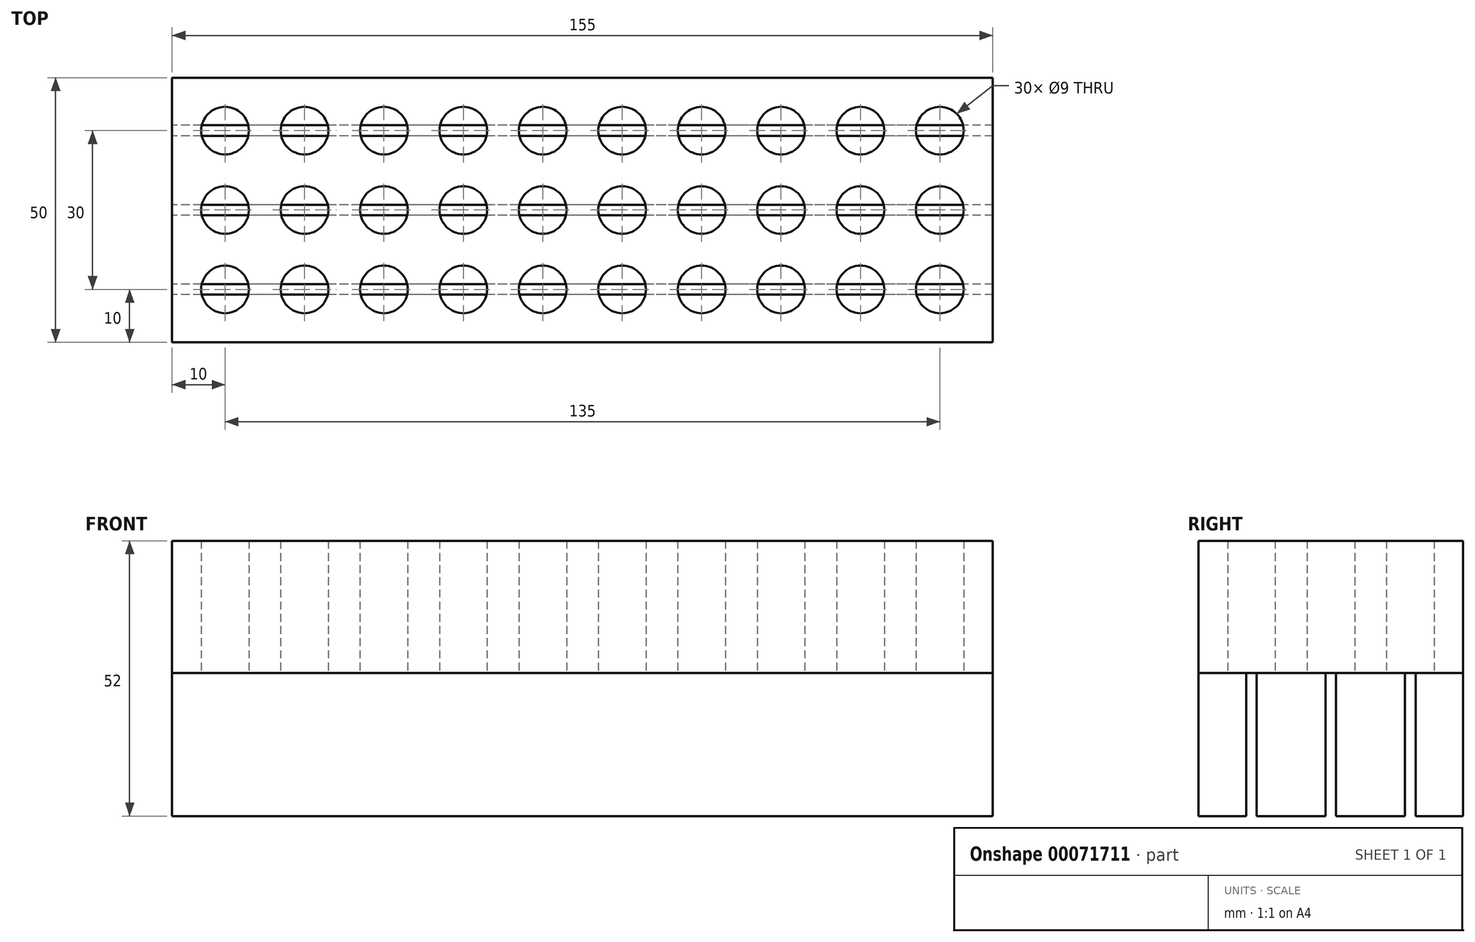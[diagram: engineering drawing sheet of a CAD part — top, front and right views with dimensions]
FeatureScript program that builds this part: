
annotation { "Feature Type Name" : "Feature", "Feature Type Description" : "" }
export const myFeature = defineFeature(function(context is Context, id is Id, definition is map)
    precondition{}
    {
        {
            var Q0;
            Q0=qCreatedBy(makeId("Top.planeOp"),FACE);
            var sketch = newSketch(context, id + "F0", { "sketchPlane" : qUnion([Q0])});
            skLineSegment(sketch, "E0.rect.bottom", {"start": v(77.5, 25) * mm, "end": v(-77.5, 25) * mm});
            skLineSegment(sketch, "E0.rect.top", {"start": v(77.5, -25) * mm, "end": v(-77.5, -25) * mm});
            skLineSegment(sketch, "E0.rect.left", {"start": v(77.5, 25) * mm, "end": v(77.5, -25) * mm});
            skLineSegment(sketch, "E0.rect.right", {"start": v(-77.5, 25) * mm, "end": v(-77.5, -25) * mm});
            skPoint(sketch, "E0.rect.middle", {"position": v(0, 0) * mm});
            skCircle(sketch, "E1", {"center": v(-67.5, 15) * mm, "radius": 4.5 * mm, "construction": true});
            skLineSegment(sketch, "E2.rect.bottom", {"start": v(77.5, 1) * mm, "end": v(-77.5, 1) * mm});
            skLineSegment(sketch, "E2.rect.top", {"start": v(77.5, -1) * mm, "end": v(-77.5, -1) * mm});
            skLineSegment(sketch, "E2.rect.left", {"start": v(77.5, 1) * mm, "end": v(77.5, -1) * mm});
            skLineSegment(sketch, "E2.rect.right", {"start": v(-77.5, 1) * mm, "end": v(-77.5, -1) * mm});
            skCircle(sketch, "E3.0.1.0", {"center": v(-67.5, 0) * mm, "radius": 4.5 * mm, "construction": true});
            skCircle(sketch, "E3.0.2.0", {"center": v(-67.5, -15) * mm, "radius": 4.5 * mm, "construction": true});
            skCircle(sketch, "E3.1.0.0", {"center": v(-52.5, 15) * mm, "radius": 4.5 * mm, "construction": true});
            skCircle(sketch, "E3.1.1.0", {"center": v(-52.5, 0) * mm, "radius": 4.5 * mm, "construction": true});
            skCircle(sketch, "E3.1.2.0", {"center": v(-52.5, -15) * mm, "radius": 4.5 * mm, "construction": true});
            skCircle(sketch, "E3.2.0.0", {"center": v(-37.5, 15) * mm, "radius": 4.5 * mm, "construction": true});
            skCircle(sketch, "E3.2.1.0", {"center": v(-37.5, 0) * mm, "radius": 4.5 * mm, "construction": true});
            skCircle(sketch, "E3.2.2.0", {"center": v(-37.5, -15) * mm, "radius": 4.5 * mm, "construction": true});
            skCircle(sketch, "E3.3.0.0", {"center": v(-22.5, 15) * mm, "radius": 4.5 * mm, "construction": true});
            skCircle(sketch, "E3.3.1.0", {"center": v(-22.5, 0) * mm, "radius": 4.5 * mm, "construction": true});
            skCircle(sketch, "E3.3.2.0", {"center": v(-22.5, -15) * mm, "radius": 4.5 * mm, "construction": true});
            skCircle(sketch, "E3.4.0.0", {"center": v(-7.5, 15) * mm, "radius": 4.5 * mm, "construction": true});
            skCircle(sketch, "E3.4.1.0", {"center": v(-7.5, 0) * mm, "radius": 4.5 * mm, "construction": true});
            skCircle(sketch, "E3.4.2.0", {"center": v(-7.5, -15) * mm, "radius": 4.5 * mm, "construction": true});
            skCircle(sketch, "E3.5.0.0", {"center": v(7.5, 15) * mm, "radius": 4.5 * mm, "construction": true});
            skCircle(sketch, "E3.5.1.0", {"center": v(7.5, 0) * mm, "radius": 4.5 * mm, "construction": true});
            skCircle(sketch, "E3.5.2.0", {"center": v(7.5, -15) * mm, "radius": 4.5 * mm, "construction": true});
            skCircle(sketch, "E3.6.0.0", {"center": v(22.5, 15) * mm, "radius": 4.5 * mm, "construction": true});
            skCircle(sketch, "E3.6.1.0", {"center": v(22.5, 0) * mm, "radius": 4.5 * mm, "construction": true});
            skCircle(sketch, "E3.6.2.0", {"center": v(22.5, -15) * mm, "radius": 4.5 * mm, "construction": true});
            skCircle(sketch, "E3.7.0.0", {"center": v(37.5, 15) * mm, "radius": 4.5 * mm, "construction": true});
            skCircle(sketch, "E3.7.1.0", {"center": v(37.5, 0) * mm, "radius": 4.5 * mm, "construction": true});
            skCircle(sketch, "E3.7.2.0", {"center": v(37.5, -15) * mm, "radius": 4.5 * mm, "construction": true});
            skCircle(sketch, "E3.8.0.0", {"center": v(52.5, 15) * mm, "radius": 4.5 * mm, "construction": true});
            skCircle(sketch, "E3.8.1.0", {"center": v(52.5, 0) * mm, "radius": 4.5 * mm, "construction": true});
            skCircle(sketch, "E3.8.2.0", {"center": v(52.5, -15) * mm, "radius": 4.5 * mm, "construction": true});
            skCircle(sketch, "E3.9.0.0", {"center": v(67.5, 15) * mm, "radius": 4.5 * mm, "construction": true});
            skCircle(sketch, "E3.9.1.0", {"center": v(67.5, 0) * mm, "radius": 4.5 * mm, "construction": true});
            skCircle(sketch, "E3.9.2.0", {"center": v(67.5, -15) * mm, "radius": 4.5 * mm, "construction": true});
            skLineSegment(sketch, "E3.direction1", {"start": v(-67.5, 15) * mm, "end": v(-52.5, 15) * mm, "construction": true});
            skLineSegment(sketch, "E3.direction2", {"start": v(-67.5, 15) * mm, "end": v(-67.5, 0) * mm, "construction": true});
            skLineSegment(sketch, "E4.rect.bottom", {"start": v(77.5, 14) * mm, "end": v(-77.5, 14) * mm});
            skLineSegment(sketch, "E4.rect.top", {"start": v(77.5, 16) * mm, "end": v(-77.5, 16) * mm});
            skLineSegment(sketch, "E4.rect.left", {"start": v(77.5, 14) * mm, "end": v(77.5, 16) * mm});
            skLineSegment(sketch, "E4.rect.right", {"start": v(-77.5, 14) * mm, "end": v(-77.5, 16) * mm});
            skPoint(sketch, "E4.rect.middle", {"position": v(0, 15) * mm});
            skPoint(sketch, "E4.rect.middle.positionSnap0", {"position": v(0, 25) * mm});
            skPoint(sketch, "E4.rect.centerSnap0", {"position": v(0, 25) * mm});
            skLineSegment(sketch, "E5.rect.bottom", {"start": v(77.5, -16) * mm, "end": v(-77.5, -16) * mm});
            skLineSegment(sketch, "E5.rect.top", {"start": v(77.5, -14) * mm, "end": v(-77.5, -14) * mm});
            skLineSegment(sketch, "E5.rect.left", {"start": v(77.5, -16) * mm, "end": v(77.5, -14) * mm});
            skLineSegment(sketch, "E5.rect.right", {"start": v(-77.5, -16) * mm, "end": v(-77.5, -14) * mm});
            skPoint(sketch, "E5.rect.middle", {"position": v(0, -15) * mm});
            skPoint(sketch, "E5.rect.middle.positionSnap0", {"position": v(0, -25) * mm});
            skPoint(sketch, "E5.rect.centerSnap0", {"position": v(0, -25) * mm});
            skSolve(sketch);
        }
        {
            var Q0;
            {var subQ0=sQuery(id+"F0.wireOp",EDGE,"E0.rect.bottom");Q0=makeQuery(id+"F0.imprint","IMPRINT",FACE,{"disambiguationData":[TD([[makeQuery(id+"F0.imprint","IMPRINT",EDGE,{"derivedFrom":subQ0}),1.0]])]});}
            var Q1;
            {var subQ0=sQuery(id+"F0.wireOp",EDGE,"E0.rect.top");Q1=makeQuery(id+"F0.imprint","IMPRINT",FACE,{"disambiguationData":[TD([[makeQuery(id+"F0.imprint","IMPRINT",EDGE,{"derivedFrom":subQ0}),-1.0]])]});}
            var Q2;
            {var subQ0=sQuery(id+"F0.wireOp",EDGE,"E2.rect.bottom");Q2=makeQuery(id+"F0.imprint","IMPRINT",FACE,{"disambiguationData":[TD([[makeQuery(id+"F0.imprint","IMPRINT",EDGE,{"derivedFrom":subQ0}),-1.0]])]});}
            var Q3;
            {var subQ0=sQuery(id+"F0.wireOp",EDGE,"E2.rect.top");Q3=makeQuery(id+"F0.imprint","IMPRINT",FACE,{"disambiguationData":[TD([[makeQuery(id+"F0.imprint","IMPRINT",EDGE,{"derivedFrom":subQ0}),1.0]])]});}
            extrude(context, id + "F1", {"entities" : qUnion([Q0, Q1, Q2, Q3]), "depth" : 27 * mm});
        }
        {
            var Q0;
            Q0=makeQuery(id+"F1.opExtrude","CAP_FACE",FACE,{"disambiguationData":[OSD([sQuery(id+"F0.wireOp",EDGE,"E0.rect.left"),sQuery(id+"F0.wireOp",EDGE,"E0.rect.right"),sQuery(id+"F0.wireOp",EDGE,"E2.rect.bottom"),sQuery(id+"F0.wireOp",EDGE,"E4.rect.bottom")])],"isStart":false});
            var sketch = newSketch(context, id + "F2", { "sketchPlane" : qUnion([Q0])});
            skLineSegment(sketch, "E6.0.0", {"start": v(-77.5, -25) * mm, "end": v(77.5, -25) * mm});
            skLineSegment(sketch, "E6.0.1", {"start": v(77.5, -25) * mm, "end": v(77.5, -16) * mm});
            skLineSegment(sketch, "E6.0.3", {"start": v(-77.5, -16) * mm, "end": v(-77.5, -25) * mm});
            skLineSegment(sketch, "E7.0.0", {"start": v(77.5, -14) * mm, "end": v(77.5, -1) * mm});
            skLineSegment(sketch, "E7.0.2", {"start": v(-77.5, -1) * mm, "end": v(-77.5, -14) * mm});
            skLineSegment(sketch, "E8.0.0", {"start": v(77.5, 1) * mm, "end": v(77.5, 14) * mm});
            skLineSegment(sketch, "E8.0.2", {"start": v(-77.5, 14) * mm, "end": v(-77.5, 1) * mm});
            skLineSegment(sketch, "E9.0.0", {"start": v(77.5, 16) * mm, "end": v(77.5, 25) * mm});
            skLineSegment(sketch, "E9.0.1", {"start": v(77.5, 25) * mm, "end": v(-77.5, 25) * mm});
            skLineSegment(sketch, "E9.0.2", {"start": v(-77.5, 25) * mm, "end": v(-77.5, 16) * mm});
            skCircle(sketch, "E10.0", {"center": v(-67.5, 15) * mm, "radius": 4.5 * mm});
            skCircle(sketch, "E11.0", {"center": v(-67.5, 0) * mm, "radius": 4.5 * mm});
            skCircle(sketch, "E12.0", {"center": v(-67.5, -15) * mm, "radius": 4.5 * mm});
            skCircle(sketch, "E13.0", {"center": v(-52.5, -15) * mm, "radius": 4.5 * mm});
            skCircle(sketch, "E14.0", {"center": v(-52.5, 15) * mm, "radius": 4.5 * mm});
            skCircle(sketch, "E15.0", {"center": v(-37.5, -15) * mm, "radius": 4.5 * mm});
            skCircle(sketch, "E16.0", {"center": v(-52.5, 0) * mm, "radius": 4.5 * mm});
            skCircle(sketch, "E17.0", {"center": v(-37.5, 0) * mm, "radius": 4.5 * mm});
            skCircle(sketch, "E18.0", {"center": v(-37.5, 15) * mm, "radius": 4.5 * mm});
            skCircle(sketch, "E19.0", {"center": v(-22.5, 15) * mm, "radius": 4.5 * mm});
            skCircle(sketch, "E20.0", {"center": v(-22.5, 0) * mm, "radius": 4.5 * mm});
            skCircle(sketch, "E21.0", {"center": v(-22.5, -15) * mm, "radius": 4.5 * mm});
            skCircle(sketch, "E22.0", {"center": v(-7.5, -15) * mm, "radius": 4.5 * mm});
            skCircle(sketch, "E23.0", {"center": v(-7.5, 0) * mm, "radius": 4.5 * mm});
            skCircle(sketch, "E24.0", {"center": v(-7.5, 15) * mm, "radius": 4.5 * mm});
            skCircle(sketch, "E25.0", {"center": v(7.5, 15) * mm, "radius": 4.5 * mm});
            skCircle(sketch, "E26.0", {"center": v(7.5, 0) * mm, "radius": 4.5 * mm});
            skCircle(sketch, "E27.0", {"center": v(7.5, -15) * mm, "radius": 4.5 * mm});
            skCircle(sketch, "E28.0", {"center": v(22.5, -15) * mm, "radius": 4.5 * mm});
            skCircle(sketch, "E29.0", {"center": v(22.5, 0) * mm, "radius": 4.5 * mm});
            skCircle(sketch, "E30.0", {"center": v(22.5, 15) * mm, "radius": 4.5 * mm});
            skCircle(sketch, "E31.0", {"center": v(37.5, 15) * mm, "radius": 4.5 * mm});
            skCircle(sketch, "E32.0", {"center": v(37.5, 0) * mm, "radius": 4.5 * mm});
            skCircle(sketch, "E33.0", {"center": v(37.5, -15) * mm, "radius": 4.5 * mm});
            skCircle(sketch, "E34.0", {"center": v(52.5, -15) * mm, "radius": 4.5 * mm});
            skCircle(sketch, "E35.0", {"center": v(52.5, 0) * mm, "radius": 4.5 * mm});
            skCircle(sketch, "E36.0", {"center": v(52.5, 15) * mm, "radius": 4.5 * mm});
            skCircle(sketch, "E37.0", {"center": v(67.5, 15) * mm, "radius": 4.5 * mm});
            skCircle(sketch, "E38.0", {"center": v(67.5, 0) * mm, "radius": 4.5 * mm});
            skCircle(sketch, "E39.0", {"center": v(67.5, -15) * mm, "radius": 4.5 * mm});
            skLineSegment(sketch, "E40.0", {"start": v(77.5, 25) * mm, "end": v(77.5, -25) * mm});
            skLineSegment(sketch, "E41.0", {"start": v(77.5, 1) * mm, "end": v(77.5, -1) * mm});
            skLineSegment(sketch, "E42.0", {"start": v(-77.5, 25) * mm, "end": v(-77.5, -25) * mm});
            skSolve(sketch);
        }
        {
            var Q0;
            Q0 = qSketchRegion(id + "F2", true);
            extrude(context, id + "F3", {"entities" : qUnion([Q0]), "depth" : 25 * mm});
        }
    });
